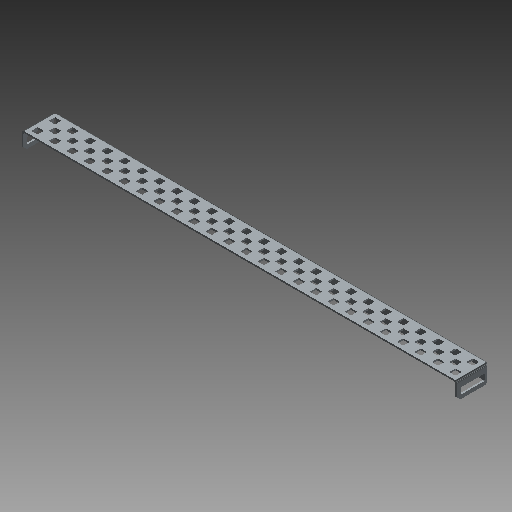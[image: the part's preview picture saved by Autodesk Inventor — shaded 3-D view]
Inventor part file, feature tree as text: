
AUTODESK INVENTOR PART (.ipt)
format: ipt  version: 2018 (Build 220112000, 112)  size: 1,925,632 bytes
history: native  units: mm (DEFAULTED — no unit token found)
features: other x103, extrude x103, sketch x4, pattern_linear x3, imported_body x1
ambient origin geometry x8: Origin, YZ Plane, XZ Plane, XY Plane, X Axis, Y Axis, Z Axis, Center Point
bodies: Solid1 (feature_tree)
feature tree (214):
  imported_body  "Base1"
  sketch  "Sketch1"  dims[d2=1.1684mm]
  pattern_linear  "Rectangular Pattern1"  Count1=25  [1 undecoded]
  pattern_linear  "Rectangular Pattern2"  Spacing1=12.7mm  [1 undecoded]
  sketch  "Sketch2"  dims[d3=0.0mm]
  sketch  "Sketch3"  dims[d4=1.1684mm]
  pattern_linear  "Rectangular Pattern3"  Count1=2 Spacing1=12.7mm
  other  "Srf1"
  other  "Srf2"
  other  "Srf3"
  other  "Srf4"
  other  "Srf5"
  other  "Srf6"
  other  "Srf7"
  other  "Srf8"
  other  "Srf9"
  other  "Srf10"
  other  "Srf11"
  other  "Srf12"
  other  "Srf13"
  other  "Srf14"
  other  "Srf15"
  other  "Srf16"
  other  "Srf17"
  other  "Srf18"
  other  "Srf19"
  other  "Srf20"
  other  "Srf21"
  other  "Srf22"
  other  "Srf23"
  other  "Srf24"
  other  "Srf25"
  other  "Srf26"
  other  "Srf27"
  other  "Srf28"
  other  "Srf29"
  other  "Srf30"
  other  "Srf31"
  other  "Srf32"
  other  "Srf33"
  other  "Srf34"
  other  "Srf35"
  other  "Srf36"
  other  "Srf37"
  other  "Srf38"
  other  "Srf39"
  other  "Srf40"
  other  "Srf41"
  other  "Srf42"
  other  "Srf43"
  other  "Srf44"
  other  "Srf45"
  other  "Srf46"
  other  "Srf47"
  other  "Srf48"
  other  "Srf49"
  other  "Srf50"
  other  "Srf51"
  other  "Srf52"
  other  "Srf53"
  other  "Srf54"
  other  "Srf55"
  other  "Srf56"
  other  "Srf57"
  other  "Srf58"
  other  "Srf59"
  other  "Srf60"
  other  "Srf61"
  other  "Srf62"
  other  "Srf63"
  other  "Srf64"
  other  "Srf65"
  other  "Srf66"
  other  "Srf67"
  other  "Srf68"
  other  "Srf69"
  other  "Srf70"
  other  "Srf71"
  other  "Srf72"
  other  "Srf73"
  other  "Srf74"
  other  "Srf75"
  other  "Srf76"
  other  "Srf77"
  other  "Srf78"
  sketch  "Sketch4"  dims[d5=0.0mm d6=250.0mm d8=12.7mm d9=20.0mm d11=12.7mm d12=240.0mm d14=12.7mm d15=1.1684mm d16=0.0mm d17=1.1684mm d18=0.0mm d19=1.1684mm d20=0.0mm d21=1.1684mm d22=0.0mm d23=1.1684mm d24=0.0mm d25=250.0mm d27=12.7mm d28=0.0mm d29=0.0mm d30=0.0mm d31=0.0mm d32=0.0mm d33=0.0mm d34=0.0mm d35=0.0mm d36=0.0mm d37=0.0mm d38=0.0mm d39=0.0mm d40=0.0mm d41=0.0mm d42=0.0mm d43=0.0mm d44=0.0mm d45=0.0mm d46=0.0mm d47=0.0mm d48=0.0mm d49=0.0mm d50=0.0mm d51=0.0mm d52=0.0mm d53=0.0mm d54=0.0mm d55=0.0mm d56=0.0mm d57=0.0mm d58=0.0mm d59=0.0mm d60=0.0mm d61=0.0mm d62=0.0mm d63=0.0mm d64=0.0mm d65=0.0mm d66=0.0mm d67=0.0mm d68=0.0mm d69=0.0mm d70=0.0mm d71=0.0mm d72=0.0mm d73=0.0mm d74=0.0mm d75=0.0mm d76=0.0mm d77=0.0mm d78=0.0mm d79=0.0mm d80=0.0mm d81=0.0mm d82=0.0mm d83=0.0mm d84=0.0mm d85=0.0mm d86=0.0mm d87=0.0mm d88=0.0mm d89=0.0mm d90=0.0mm d91=0.0mm d92=0.0mm d93=0.0mm d94=0.0mm d95=0.0mm d96=0.0mm d97=0.0mm d98=0.0mm d99=0.0mm d100=0.0mm d101=0.0mm d102=0.0mm d103=0.0mm d104=0.0mm d105=0.0mm d106=0.0mm d107=0.0mm d108=0.0mm d109=0.0mm d110=0.0mm d111=0.0mm d112=0.0mm d113=0.0mm d114=0.0mm d115=0.0mm d116=0.0mm d117=0.0mm d118=0.0mm d119=0.0mm d120=0.0mm d121=0.0mm d122=0.0mm d123=0.0mm d124=0.0mm d125=0.0mm d126=0.0mm d127=0.0mm d128=0.0mm d129=0.0mm d130=0.0mm d131=0.0mm d132=0.0mm d133=0.0mm d134=0.0mm d135=0.0mm d136=0.0mm d137=0.0mm d138=0.0mm d139=0.0mm d140=0.0mm d141=0.0mm d142=0.0mm d143=0.0mm d144=0.0mm d145=0.0mm d146=0.0mm d147=0.0mm d148=0.0mm d149=0.0mm d150=0.0mm d151=0.0mm d152=0.0mm d153=0.0mm d154=0.0mm d155=0.0mm d156=0.0mm d157=0.0mm d158=0.0mm d159=0.0mm d160=0.0mm d161=0.0mm d162=0.0mm d163=0.0mm d164=0.0mm d165=0.0mm d166=0.0mm d167=0.0mm d168=0.0mm d169=0.0mm d170=0.0mm d171=0.0mm d172=0.0mm d173=0.0mm d174=0.0mm d175=0.0mm d176=0.0mm d177=0.0mm d178=0.0mm d179=0.0mm d180=0.0mm d181=0.0mm d182=0.0mm d183=0.0mm d184=0.0mm d185=0.0mm d186=0.0mm d187=0.0mm d188=0.0mm d189=0.0mm d190=0.0mm d191=0.0mm d192=0.0mm d193=0.0mm d194=0.0mm d195=0.0mm d196=0.0mm d197=0.0mm d198=0.0mm d199=0.0mm d200=0.0mm d201=0.0mm d202=0.0mm d203=0.0mm d204=0.0mm d205=0.0mm d206=0.0mm d207=0.0mm d208=0.0mm d209=0.0mm d210=0.0mm d211=0.0mm d212=0.0mm d213=0.0mm d214=0.0mm d215=0.0mm d216=0.0mm d217=0.0mm d218=0.0mm d219=0.0mm d220=0.0mm d221=0.0mm d222=0.0mm d223=0.0mm d224=0.0mm d225=0.0mm d226=0.0mm d227=0.0mm d228=0.0mm d229=0.0mm d230=0.0mm d231=0.0mm d232=0.0mm d233=0.0mm]
  other  "Srf79"
  other  "Srf80"
  other  "Srf81"
  other  "Srf82"
  other  "Srf83"
  other  "Srf84"
  other  "Srf85"
  other  "Srf86"
  other  "Srf87"
  other  "Srf88"
  other  "Srf89"
  other  "Srf90"
  other  "Srf91"
  other  "Srf92"
  other  "Srf93"
  other  "Srf94"
  other  "Srf95"
  other  "Srf96"
  other  "Srf97"
  other  "Srf98"
  other  "Srf99"
  other  "Srf100"
  other  "Srf101"
  other  "Srf102"
  other  "Srf103"
  extrude  "ExtrusionSrf1"  Depth=240.0mm
  extrude  "ExtrusionSrf2"  Depth=12.7mm
  extrude  "ExtrusionSrf75"  Depth=1.1684mm
  extrude  "ExtrusionSrf76"  TaperAngle=0.0deg  [1 undecoded]
  extrude  "ExtrusionSrf77"  Depth=1.1684mm
  extrude  "ExtrusionSrf78"  TaperAngle=0.0deg  [1 undecoded]
  extrude  "ExtrusionSrf79"  Depth=1.1684mm
  extrude  "ExtrusionSrf3"  TaperAngle=0.0deg  [1 undecoded]
  extrude  "ExtrusionSrf4"  Depth=1.1684mm
  extrude  "ExtrusionSrf5"  TaperAngle=0.0deg  [1 undecoded]
  extrude  "ExtrusionSrf6"  Depth=1.1684mm
  extrude  "ExtrusionSrf7"  TaperAngle=0.0deg  [1 undecoded]
  extrude  "ExtrusionSrf8"  Depth=250.0mm
  extrude  "ExtrusionSrf9"  Depth=12.7mm
  extrude  "ExtrusionSrf10"  [1 undecoded]
  extrude  "ExtrusionSrf11"  [1 undecoded]
  extrude  "ExtrusionSrf12"  [1 undecoded]
  extrude  "ExtrusionSrf13"  [1 undecoded]
  extrude  "ExtrusionSrf14"  [1 undecoded]
  extrude  "ExtrusionSrf15"  [1 undecoded]
  extrude  "ExtrusionSrf16"  [1 undecoded]
  extrude  "ExtrusionSrf17"  [1 undecoded]
  extrude  "ExtrusionSrf18"  [1 undecoded]
  extrude  "ExtrusionSrf19"  [1 undecoded]
  extrude  "ExtrusionSrf20"  [1 undecoded]
  extrude  "ExtrusionSrf21"  [1 undecoded]
  extrude  "ExtrusionSrf22"  [1 undecoded]
  extrude  "ExtrusionSrf23"  [1 undecoded]
  extrude  "ExtrusionSrf24"  [1 undecoded]
  extrude  "ExtrusionSrf25"  [1 undecoded]
  extrude  "ExtrusionSrf26"  [1 undecoded]
  extrude  "ExtrusionSrf27"  [1 undecoded]
  extrude  "ExtrusionSrf28"  [1 undecoded]
  extrude  "ExtrusionSrf29"  [1 undecoded]
  extrude  "ExtrusionSrf30"  [1 undecoded]
  extrude  "ExtrusionSrf31"  [1 undecoded]
  extrude  "ExtrusionSrf32"  [1 undecoded]
  extrude  "ExtrusionSrf33"  [1 undecoded]
  extrude  "ExtrusionSrf34"  [1 undecoded]
  extrude  "ExtrusionSrf35"  [1 undecoded]
  extrude  "ExtrusionSrf36"  [1 undecoded]
  extrude  "ExtrusionSrf37"  [1 undecoded]
  extrude  "ExtrusionSrf38"  [1 undecoded]
  extrude  "ExtrusionSrf39"  [1 undecoded]
  extrude  "ExtrusionSrf40"  [1 undecoded]
  extrude  "ExtrusionSrf41"  [1 undecoded]
  extrude  "ExtrusionSrf42"  [1 undecoded]
  extrude  "ExtrusionSrf43"  [1 undecoded]
  extrude  "ExtrusionSrf44"  [1 undecoded]
  extrude  "ExtrusionSrf45"  [1 undecoded]
  extrude  "ExtrusionSrf46"  [1 undecoded]
  extrude  "ExtrusionSrf47"  [1 undecoded]
  extrude  "ExtrusionSrf48"  [1 undecoded]
  extrude  "ExtrusionSrf49"  [1 undecoded]
  extrude  "ExtrusionSrf50"  [1 undecoded]
  extrude  "ExtrusionSrf51"  [1 undecoded]
  extrude  "ExtrusionSrf52"  [1 undecoded]
  extrude  "ExtrusionSrf53"  [1 undecoded]
  extrude  "ExtrusionSrf54"  [1 undecoded]
  extrude  "ExtrusionSrf55"  [1 undecoded]
  extrude  "ExtrusionSrf56"  [1 undecoded]
  extrude  "ExtrusionSrf57"  [1 undecoded]
  extrude  "ExtrusionSrf58"  [1 undecoded]
  extrude  "ExtrusionSrf59"  [1 undecoded]
  extrude  "ExtrusionSrf60"  [1 undecoded]
  extrude  "ExtrusionSrf61"  [1 undecoded]
  extrude  "ExtrusionSrf62"  [1 undecoded]
  extrude  "ExtrusionSrf63"  [1 undecoded]
  extrude  "ExtrusionSrf64"  [1 undecoded]
  extrude  "ExtrusionSrf65"  [1 undecoded]
  extrude  "ExtrusionSrf66"  [1 undecoded]
  extrude  "ExtrusionSrf67"  [1 undecoded]
  extrude  "ExtrusionSrf68"  [1 undecoded]
  extrude  "ExtrusionSrf69"  [1 undecoded]
  extrude  "ExtrusionSrf70"  [1 undecoded]
  extrude  "ExtrusionSrf71"  [1 undecoded]
  extrude  "ExtrusionSrf72"  [1 undecoded]
  extrude  "ExtrusionSrf73"  [1 undecoded]
  extrude  "ExtrusionSrf74"  [1 undecoded]
  extrude  "ExtrusionSrf80"  [1 undecoded]
  extrude  "ExtrusionSrf81"  [1 undecoded]
  extrude  "ExtrusionSrf82"  [1 undecoded]
  extrude  "ExtrusionSrf83"  [1 undecoded]
  extrude  "ExtrusionSrf84"  [1 undecoded]
  extrude  "ExtrusionSrf85"  [1 undecoded]
  extrude  "ExtrusionSrf86"  [1 undecoded]
  extrude  "ExtrusionSrf87"  [1 undecoded]
  extrude  "ExtrusionSrf88"  [1 undecoded]
  extrude  "ExtrusionSrf89"  [1 undecoded]
  extrude  "ExtrusionSrf90"  [1 undecoded]
  extrude  "ExtrusionSrf91"  [1 undecoded]
  extrude  "ExtrusionSrf92"  [1 undecoded]
  extrude  "ExtrusionSrf93"  [1 undecoded]
  extrude  "ExtrusionSrf94"  [1 undecoded]
  extrude  "ExtrusionSrf95"  [1 undecoded]
  extrude  "ExtrusionSrf96"  [1 undecoded]
  extrude  "ExtrusionSrf97"  [1 undecoded]
  extrude  "ExtrusionSrf98"  [1 undecoded]
  extrude  "ExtrusionSrf99"  [1 undecoded]
  extrude  "ExtrusionSrf100"  [1 undecoded]
  extrude  "ExtrusionSrf101"  [1 undecoded]
  extrude  "ExtrusionSrf102"  [1 undecoded]
  extrude  "ExtrusionSrf103"  [1 undecoded]
note: 96 required parameter values undecoded (feature->parameter linkage not recoverable at this tier; creation-order binding heuristic only, values carry confidence <= 0.55)
